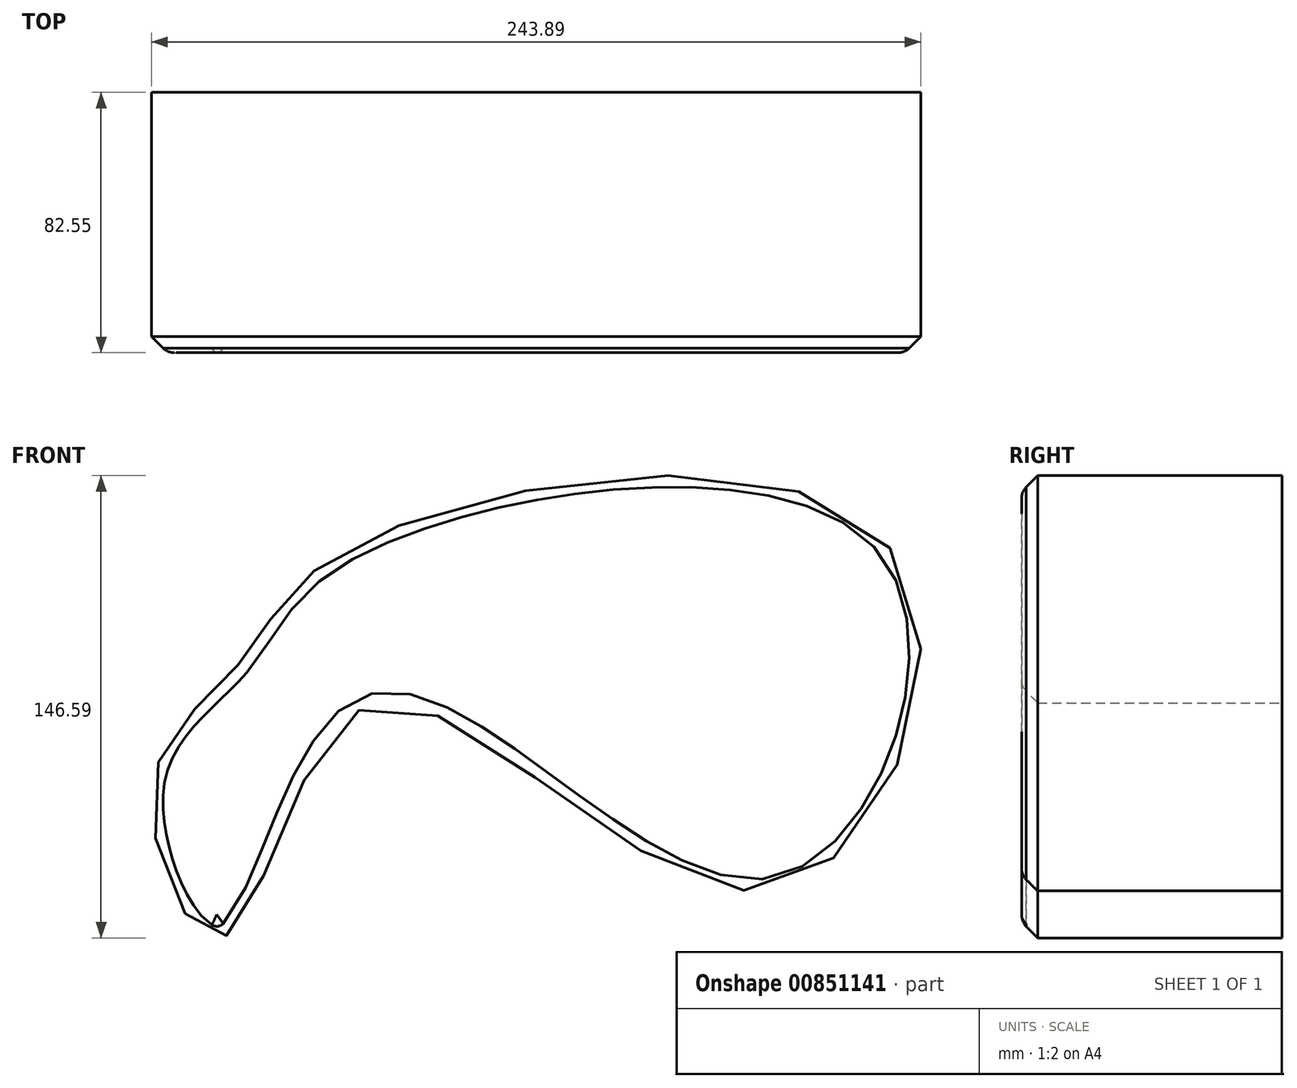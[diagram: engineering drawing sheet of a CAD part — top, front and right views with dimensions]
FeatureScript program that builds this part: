
annotation { "Feature Type Name" : "Feature", "Feature Type Description" : "" }
export const myFeature = defineFeature(function(context is Context, id is Id, definition is map)
    precondition{}
    {
        {
            var Q0;
            Q0=qCreatedBy(makeId("Front.planeOp"),FACE);
            var sketch = newSketch(context, id + "F0", { "sketchPlane" : qUnion([Q0])});
            skFitSpline(sketch, "E0", {"points": [v(-101.74, 25.52) * mm, v(-67.01, 62.35) * mm, v(105.7, 61.63) * mm, v(66.08, -45.84) * mm, v(-60.25, 12.56) * mm, v(-106.63, -60.73) * mm, v(-129.01, -14.28) * mm, v(-101.74, 25.52) * mm]});
            skSolve(sketch);
        }
        {
            var Q0;
            Q0 = qSketchRegion(id + "F0", true);
            extrude(context, id + "F1", {"entities" : qUnion([Q0]), "depth" : 82.55 * mm, "offsetDistance" : 25.4 * mm});
        }
        {
            var Q0;
            Q0=makeQuery(id+"F1.opExtrude","CAP_EDGE",EDGE,{"disambiguationData":[OSD([sQuery(id+"F0.wireOp",EDGE,"E0")])],"isStart":false});
            chamfer(context, id + "F2", {"entities" : qUnion([Q0]), "width" : 5.08 * mm, "tangentPropagation" : true});
        }
        {
            var Q0;
            {var subQ0=sQuery(id+"F0.wireOp",EDGE,"E0");Q0=makeQuery(id+"F2.opChamfer","BLEND_EDGE",EDGE,{"blendedFrom":[makeQuery(id+"F1.opExtrude","CAP_EDGE",EDGE,{"disambiguationData":[OSD([subQ0])],"isStart":false}),makeQuery(id+"F1.opExtrude","CAP_FACE",FACE,{"disambiguationData":[OSD([subQ0])],"isStart":false})],"blendedInto":[makeQuery(id+"F1.opExtrude","CAP_FACE",FACE,{"disambiguationData":[OSD([subQ0])],"isStart":false})]});}
            fillet(context, id + "F3", {"entities" : qUnion([Q0]), "radius" : 5.08 * mm, "tangentPropagation" : true, "allowEdgeOverflow" : false});
        }
    });
